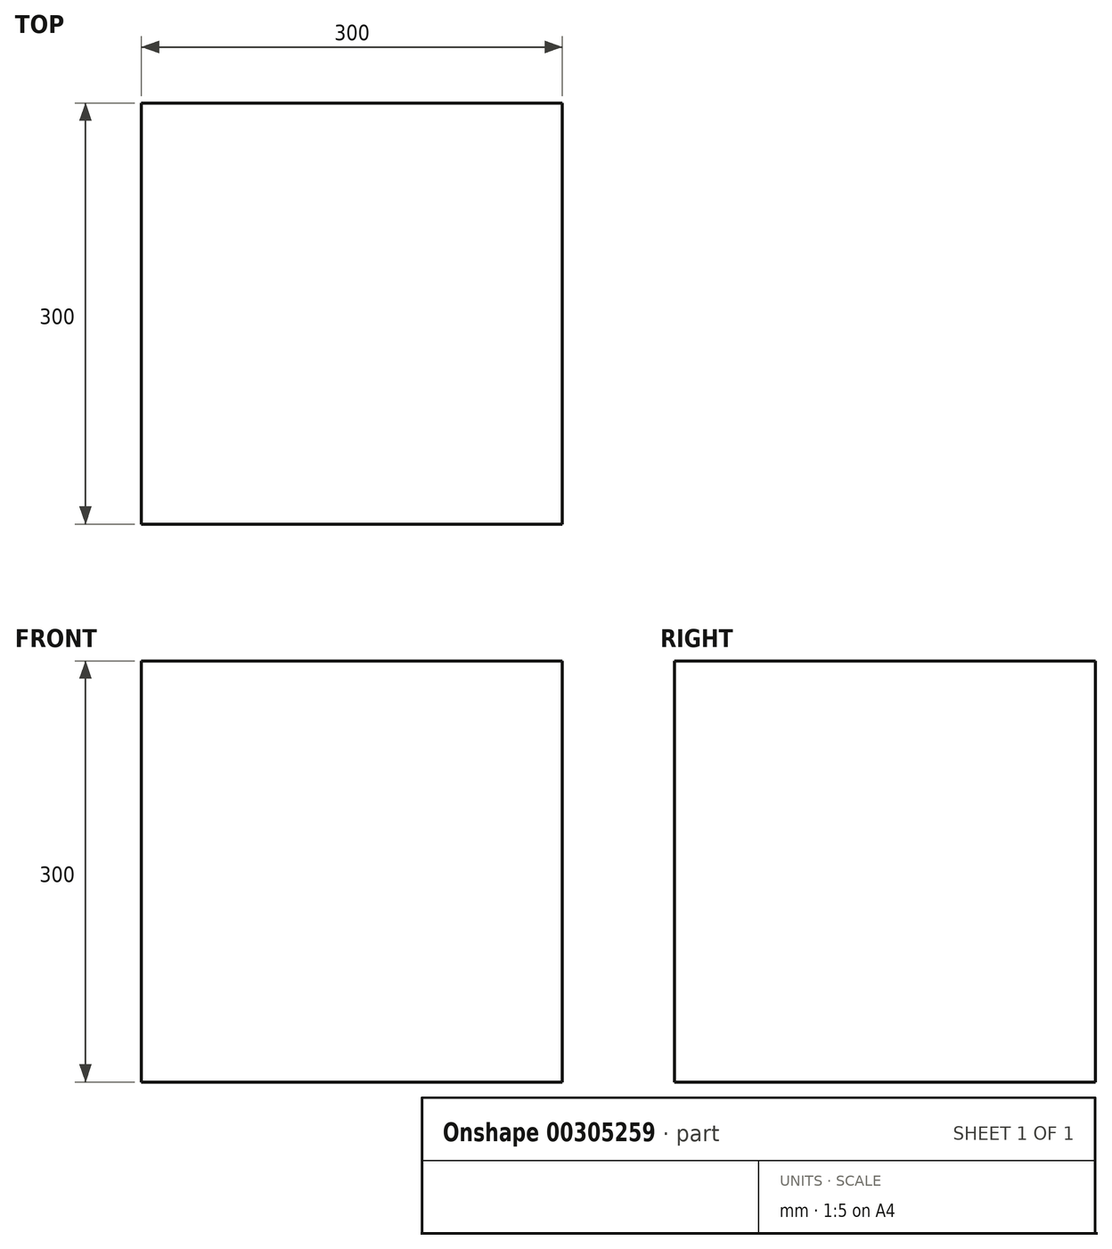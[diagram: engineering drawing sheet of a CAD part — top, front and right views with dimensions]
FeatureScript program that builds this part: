
annotation { "Feature Type Name" : "Feature", "Feature Type Description" : "" }
export const myFeature = defineFeature(function(context is Context, id is Id, definition is map)
    precondition{}
    {
        {
            var Q0;
            Q0=qCreatedBy(makeId("Top.planeOp"),FACE);
            var sketch = newSketch(context, id + "F0", { "sketchPlane" : qUnion([Q0])});
            skLineSegment(sketch, "E0.bottom", {"start": v(150, -150) * mm, "end": v(-150, -150) * mm});
            skLineSegment(sketch, "E0.top", {"start": v(150, 150) * mm, "end": v(-150, 150) * mm});
            skLineSegment(sketch, "E0.left", {"start": v(150, -150) * mm, "end": v(150, 150) * mm});
            skLineSegment(sketch, "E0.right", {"start": v(-150, -150) * mm, "end": v(-150, 150) * mm});
            skPoint(sketch, "E0.middle", {"position": v(0, 0) * mm});
            skSolve(sketch);
        }
        {
            var Q0;
            Q0 = qSketchRegion(id + "F0", true);
            extrude(context, id + "F1", {"entities" : qUnion([Q0]), "depth" : 300 * mm});
        }
    });
